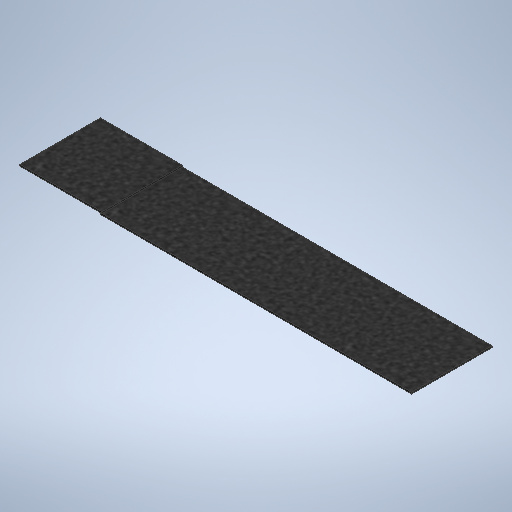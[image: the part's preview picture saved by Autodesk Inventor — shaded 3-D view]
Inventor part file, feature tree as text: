
AUTODESK INVENTOR PART (.ipt)
format: ipt  version: 2025 (Build 290162010, 162A)  size: 283,136 bytes
history: native  units: in
note: dims shown in document units (in); Inventor stores cm internally (conversion verified against a paired STEP export)
features: extrude x1, sketch x1
ambient origin geometry x8: Origin, YZ Plane, XZ Plane, XY Plane, X Axis, Y Axis, Z Axis, Center Point
bodies: Body1 (feature_tree)
feature tree (2):
  extrude  "Extrusion2"  Depth=0.125in
  sketch  "Sketch1"  dims[d0=6.5in d1=0.125in d2=0.125in d3=0.125in d4=0.125in d8=6.5in d9=0.0in d10=25.138in]
